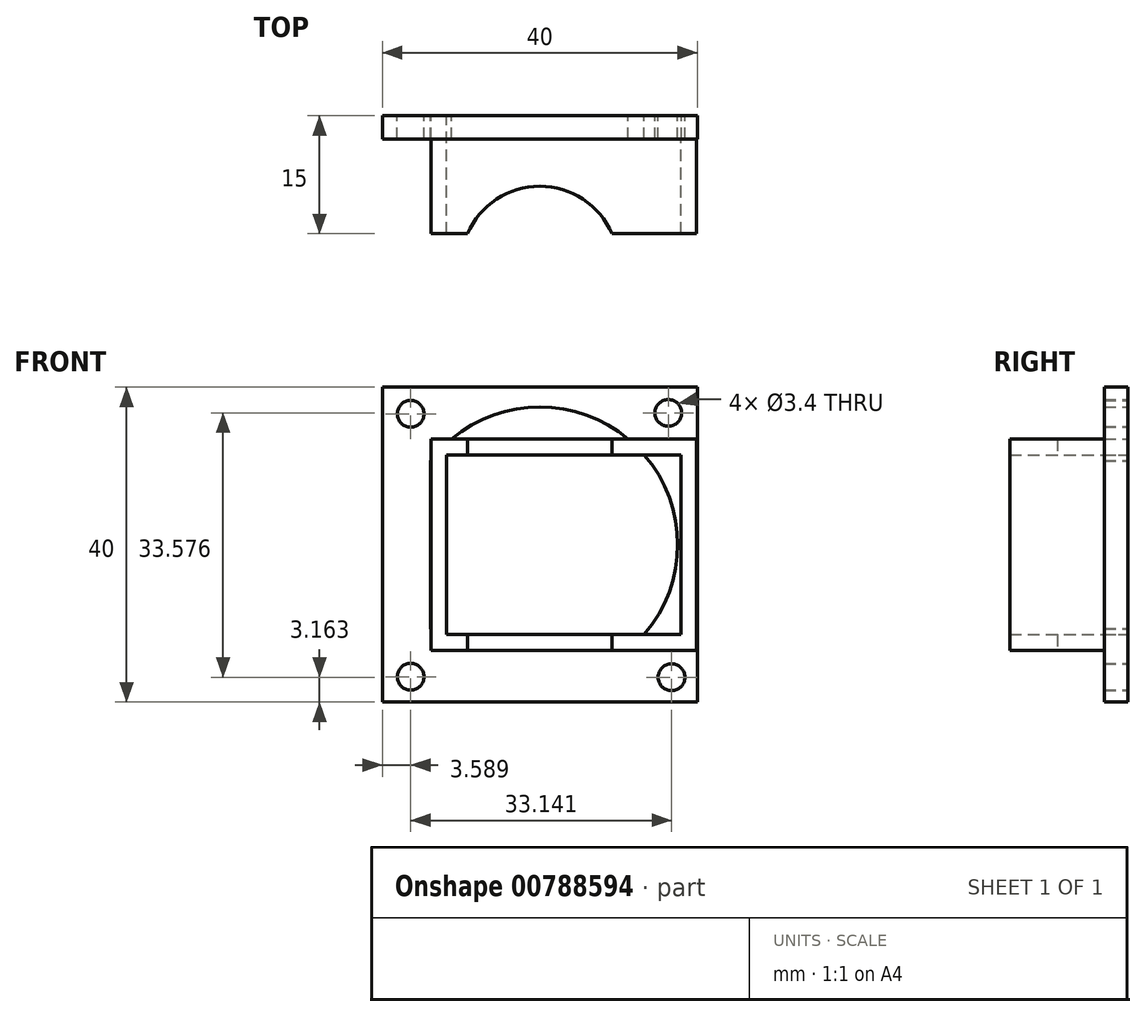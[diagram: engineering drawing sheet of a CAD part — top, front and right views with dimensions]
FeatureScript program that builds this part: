
annotation { "Feature Type Name" : "Feature", "Feature Type Description" : "" }
export const myFeature = defineFeature(function(context is Context, id is Id, definition is map)
    precondition{}
    {
        {
            var Q0;
            Q0=qCreatedBy(makeId("Front.planeOp"),FACE);
            var sketch = newSketch(context, id + "F0", { "sketchPlane" : qUnion([Q0])});
            skLineSegment(sketch, "E0.bottom", {"start": v(-13.85, 13.43) * mm, "end": v(19.91, 13.43) * mm});
            skLineSegment(sketch, "E0.top", {"start": v(-13.85, -13.43) * mm, "end": v(19.91, -13.43) * mm});
            skLineSegment(sketch, "E0.left", {"start": v(-13.85, 13.43) * mm, "end": v(-13.85, -13.43) * mm});
            skLineSegment(sketch, "E0.right", {"start": v(19.91, 13.43) * mm, "end": v(19.91, -13.43) * mm});
            skLineSegment(sketch, "E1.bottom", {"start": v(-12.47, -13.43) * mm, "end": v(12.47, -13.43) * mm});
            skLineSegment(sketch, "E1.top", {"start": v(-12.47, -19.82) * mm, "end": v(12.47, -19.82) * mm});
            skLineSegment(sketch, "E1.left", {"start": v(-12.47, -13.43) * mm, "end": v(-12.47, -19.82) * mm});
            skLineSegment(sketch, "E1.right", {"start": v(12.47, -13.43) * mm, "end": v(12.47, -19.82) * mm});
            skLineSegment(sketch, "E2.0", {"start": v(-11.85, 11.43) * mm, "end": v(17.91, 11.43) * mm});
            skLineSegment(sketch, "E2.1", {"start": v(-11.85, 11.43) * mm, "end": v(-11.85, -11.43) * mm});
            skLineSegment(sketch, "E2.2", {"start": v(-11.85, -11.43) * mm, "end": v(17.91, -11.43) * mm});
            skLineSegment(sketch, "E2.3", {"start": v(17.91, 11.43) * mm, "end": v(17.91, -11.43) * mm});
            skSolve(sketch);
        }
        {
            var Q0;
            Q0=qCreatedBy(makeId("Front.planeOp"),FACE);
            var sketch = newSketch(context, id + "F1", { "sketchPlane" : qUnion([Q0])});
            skLineSegment(sketch, "E3.bottom", {"start": v(-20, 20) * mm, "end": v(20, 20) * mm});
            skLineSegment(sketch, "E3.top", {"start": v(-20, -20) * mm, "end": v(20, -20) * mm});
            skLineSegment(sketch, "E3.left", {"start": v(-20, 20) * mm, "end": v(-20, -20) * mm});
            skLineSegment(sketch, "E3.right", {"start": v(20, 20) * mm, "end": v(20, -20) * mm});
            skCircle(sketch, "E4", {"center": v(-16.41, 16.62) * mm, "radius": 1.7 * mm});
            skCircle(sketch, "E5", {"center": v(16.32, 16.74) * mm, "radius": 1.7 * mm});
            skCircle(sketch, "E6", {"center": v(-16.41, -16.78) * mm, "radius": 1.7 * mm});
            skCircle(sketch, "E7", {"center": v(16.73, -16.84) * mm, "radius": 1.7 * mm});
            skCircle(sketch, "E8", {"center": v(0, 0) * mm, "radius": 17.5 * mm});
            skLineSegment(sketch, "E9", {"start": v(-13.89, 13.5) * mm, "end": v(-13.89, -13.48) * mm});
            skSolve(sketch);
        }
        {
            var Q0;
            Q0 = qSketchRegion(id + "F1", true);
            var Q1;
            {var subQ0=sQuery(id+"F1.wireOp",EDGE,"E9");var subQ1=sQuery(id+"F1.wireOp",EDGE,"E8");var subQ2=makeQuery(id+"F1.imprint","INTERSECT",VERTEX,{"disambiguationData":[OD(0.0)],"derivedFrom":[subQ1,subQ0]});Q1=makeQuery(id+"F1.imprint","IMPRINT",FACE,{"disambiguationData":[TD([[makeQuery(id+"F1.imprint","IMPRINT",EDGE,{"disambiguationData":[TD([[subQ2,1.0]])],"derivedFrom":subQ1}),1.0]])]});}
            extrude(context, id + "F2", {"entities" : qUnion([Q0, Q1]), "depth" : 3 * mm, "offsetDistance" : 25 * mm});
        }
        {
            var Q0;
            Q0=makeQuery(id+"F0.imprint","IMPRINT",FACE,{"disambiguationData":[TD([[makeQuery(id+"F0.imprint","IMPRINT",EDGE,{"derivedFrom":sQuery(id+"F0.wireOp",EDGE,"E0.bottom")}),-1.0]])]});
            extrude(context, id + "F3", {"entities" : qUnion([Q0]), "operationType" : NewBodyOperationType.ADD, "depth" : 15 * mm, "offsetDistance" : 25 * mm});
        }
        {
            var Q0;
            Q0=makeQuery(id+"F0.imprint","IMPRINT",FACE,{"disambiguationData":[TD([[makeQuery(id+"F0.imprint","IMPRINT",EDGE,{"derivedFrom":sQuery(id+"F0.wireOp",EDGE,"E1.top")}),1.0]])]});
            extrude(context, id + "F4", {"entities" : qUnion([Q0]), "operationType" : NewBodyOperationType.ADD, "depth" : 3 * mm, "offsetDistance" : 25 * mm});
        }
        {
            var Q0;
            Q0=qCreatedBy(makeId("Top.planeOp"),FACE);
            var sketch = newSketch(context, id + "F5", { "sketchPlane" : qUnion([Q0])});
            skCircle(sketch, "E10", {"center": v(0, -18.97) * mm, "radius": 10 * mm});
            skSolve(sketch);
        }
        {
            var Q0;
            Q0=qCreatedBy(makeId("Front.planeOp"),FACE);
            var sketch = newSketch(context, id + "F6", { "sketchPlane" : qUnion([Q0])});
            skLineSegment(sketch, "E11.bottom", {"start": v(-20.03, 13.53) * mm, "end": v(-9.27, 13.53) * mm});
            skLineSegment(sketch, "E11.top", {"start": v(-20.03, -13.21) * mm, "end": v(-9.27, -13.21) * mm});
            skLineSegment(sketch, "E11.left", {"start": v(-20.03, 13.53) * mm, "end": v(-20.03, -13.21) * mm});
            skLineSegment(sketch, "E11.right", {"start": v(-9.27, 13.53) * mm, "end": v(-9.27, -13.21) * mm});
            skLineSegment(sketch, "E12.bottom", {"start": v(20.03, 13.53) * mm, "end": v(9.27, 13.53) * mm});
            skLineSegment(sketch, "E12.top", {"start": v(20.03, -13.21) * mm, "end": v(9.27, -13.21) * mm});
            skLineSegment(sketch, "E12.left", {"start": v(20.03, 13.53) * mm, "end": v(20.03, -13.21) * mm});
            skLineSegment(sketch, "E12.right", {"start": v(9.27, 13.53) * mm, "end": v(9.27, -13.21) * mm});
            skSolve(sketch);
        }
        {
            var Q0;
            Q0=makeQuery(id+"F5.imprint","IMPRINT",FACE,{"disambiguationData":[TD([[makeQuery(id+"F5.imprint","IMPRINT",EDGE,{"derivedFrom":sQuery(id+"F5.wireOp",EDGE,"E10")}),1.0]])]});
            extrude(context, id + "F7", {"entities" : qUnion([Q0]), "operationType" : NewBodyOperationType.REMOVE, "depth" : 25 * mm, "offsetDistance" : 25 * mm, "hasSecondDirection" : true, "secondDirectionOppositeDirection" : true, "secondDirectionDepth" : 25 * mm});
        }
    });
